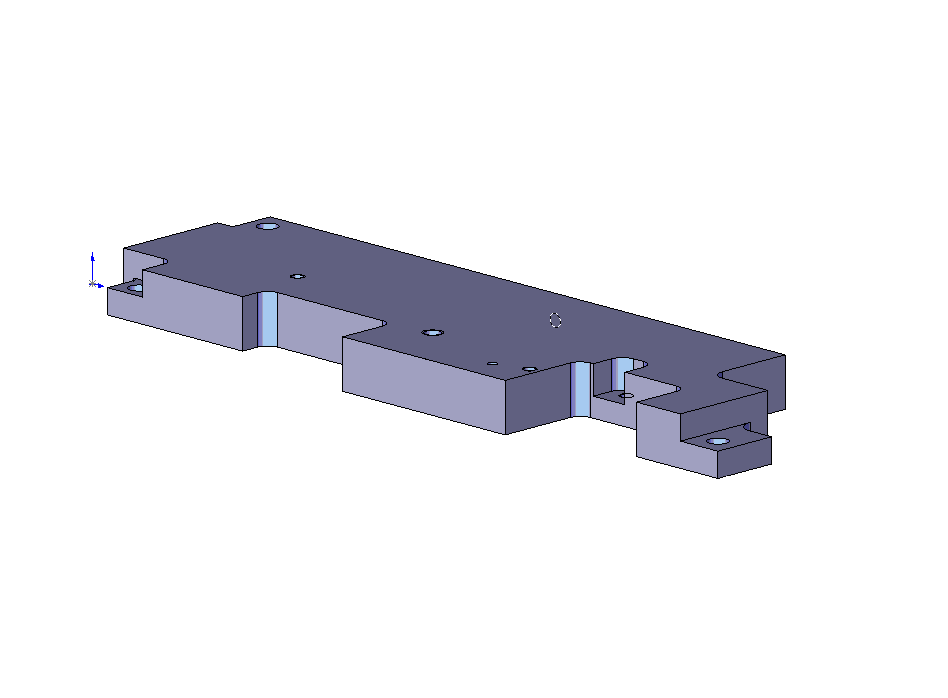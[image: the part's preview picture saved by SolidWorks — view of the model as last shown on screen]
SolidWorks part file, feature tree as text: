
SOLIDWORKS PART (.sldprt)
format: sldprt  version: not decoded by parser v0  size: 2,328,576 bytes
history: native  units: mm
features: sketch x30, cut_extrude x15, hole x6, thread x5, extrude x3, material x1, fillet x1 (+12 scaffold rows collapsed)
feature tree (73):
  scaffold x12  (default folders/planes/origin — collapsed)
  material  "Material <not specified>"
  sketch  "Sketch1"  dims[D1=16.0mm D2=500.0mm]
  extrude  "Base-Extrude"  Depth=65mm
  sketch  "Sketch3"  dims[c1.D1=10.0mm c1.D2=40.0mm c2.D1=95.0mm c2.D3=80.0mm]
  cut_extrude  "Access for Blade Clamp Bolts"  [1 undecoded]
  sketch  "Sketch2"  dims[c1.D3=20.0mm c1.D4=~11.171764mm c2.D3=4.0mm c2.D1=60.0mm c2.D2=15.0mm c3.D1=45.0mm c3.D2=30.0mm c4.D1=34.595mm c4.D2=16.0mm c4.D4=45.0mm c4.D5=60.0mm c4.D6=18.0mm c5.D5=60.0mm c5.D6=32.0mm c6.D5=60.0mm c6.D6=32.0mm c7.D5=60.0mm c7.D6=18.0mm c7.D4=45.0mm c8.D5=30.0mm c9.D5=7.0deg c9.D2=400.0mm c10.D5=400.0mm c11.D5=8.5deg c11.D4=435.0mm c11.D1=38.0mm c11.D2=40.0mm c12.D2=80.5deg c12.D4=35.0mm]
  extrude  "Boss-Extrude1"  [1 undecoded]
  sketch  "Sketch4"  dims[c1.D1=45.0mm c1.D2=35.0mm c1.D3=45.0mm c2.D1=~54.083269mm c2.D3=45.0mm c2.D4=45.0mm c3.D3=45.0mm c3.D4=45.0mm c4.D3=45.0mm c4.D4=45.0mm c5.D3=45.0mm c5.D4=45.0mm c6.D3=45.0mm c6.D4=45.0mm c7.D3=45.0mm c7.D4=45.0mm c8.D3=45.0mm c8.D4=45.0mm c9.D3=45.0mm c9.D4=45.0mm c10.D3=45.0mm c10.D4=45.0mm c11.D3=45.0mm c11.D4=45.0mm c12.D3=45.0mm c12.D4=45.0mm c13.D3=45.0mm c13.D4=45.0mm c14.D3=45.0mm c14.D4=45.0mm c15.D3=45.0mm c15.D4=45.0mm c16.D3=45.0mm c16.D4=45.0mm c17.D3=45.0mm c17.D1=45.0mm c18.D3=80.0mm]
  cut_extrude  "Cut-Extrude3"  [1 undecoded]
  sketch  "Sketch5"  dims[c1.D5=4.0mm c1.D1=100.0mm c1.D2=10.0mm c1.D3=10.0mm c2.D2=10.0mm c2.D4=40.0mm c2.D5=~38.907493mm c2.D6=~38.914066mm c3.D4=40.0mm c3.D2=40.0mm c4.D4=10.0mm]
  cut_extrude  "Cut-Extrude4"  [1 undecoded]
  sketch  "Sketch6"
  cut_extrude  "Cut-Extrude5"  [1 undecoded]
  sketch  "Sketch7"  dims[D1=10.0mm]
  extrude  "Extrude1"  [1 undecoded]
  sketch  "Sketch8"  dims[D1=4.0mm D2=65.0mm D3=42.5mm D4=30.0mm D5=10.0mm]
  cut_extrude  "Cut-Extrude6"  [1 undecoded]
  sketch  "Sketch9"
  cut_extrude  "Cut-Extrude7"  [1 undecoded]
  sketch  "Sketch10"
  cut_extrude  "Cut-Extrude8"  [1 undecoded]
  sketch  "Sketch12"  dims[c1.D1=2.8448mm c1.D3=4.1656mm c1.D2=10.0mm c2.D3=160.0mm]
  cut_extrude  "Holes for Flag"  [1 undecoded]
  sketch  "Sketch14"  dims[D1=120.0mm D2=27.5mm]
  cut_extrude  "Angled Cut"  [1 undecoded]
  hole  "1/4 Clearance Hole1"  Diameter=6.5278mm Depth=16mm
  sketch  "Sketch16"  dims[D1=12.5mm D2=7.5mm D3=6.0mm D4=12.5mm D5=20.0mm D6=7.5mm D7=7.5mm]
  sketch  "Sketch15"  dims[hole-wizard template sketch: 60 standard entries collapsed; hole parameters kept: c18.Thru Hole Depth=16.0mm]
  sketch  "Sketch17"  dims[D3=2.0mm D6=2.0mm D1=6.0mm D2=12.5mm D4=15.0mm D5=6.0mm]
  cut_extrude  "Cut-Extrude9"  [1 undecoded]
  hole  "#8-32 Tapped Hole2"  [1 undecoded]
  sketch  "3DSketch1"  dims[c1.D1=13.25mm c1.D2=~5.139942mm c1.D3=5.0mm c2.D2=78.5mm]
  thread  "Cosmetic Thread1"  Diameter=4.1656mm  [1 undecoded]
  sketch  "Sketch20"  dims[hole-wizard template sketch: 60 standard entries collapsed; hole parameters kept: c18.Thru Tap Drill Depth=16.0mm]
  sketch  "Sketch21"  dims[c1.D2=4.0mm c1.D1=20.0mm c2.D2=20.0mm]
  cut_extrude  "Cut-Extrude10"  Depth=8mm
  hole  "#8-32 Tapped Hole3"  Diameter=3.4544mm Depth=16mm
  sketch  "Sketch23"  dims[D1=194.0mm D2=39.0mm]
  sketch  "Sketch22"  dims[hole-wizard template sketch: 60 standard entries collapsed; hole parameters kept: c18.Thru Tap Drill Depth=16.0mm]
  thread  "Cosmetic Thread2"  Diameter=8.3312mm  [1 undecoded]
  hole  "1/4-20 Tapped Hole1"  Diameter=5.1054mm Depth=16mm
  sketch  "3DSketch2"  dims[D1=54.0mm D2=125.0mm]
  sketch  "Sketch25"  dims[hole-wizard template sketch: 60 standard entries collapsed; hole parameters kept: c18.Thru Tap Drill Depth=16.0mm]
  thread  "Cosmetic Thread3"  Diameter=6.35mm  [1 undecoded]
  hole  "#8-32 Tapped Hole4"  Diameter=3.4544mm Depth=12.2936mm
  sketch  "Sketch27"  dims[D1=130.0mm D2=8.0mm]
  sketch  "Sketch26"  dims[hole-wizard template sketch: 47 standard entries collapsed; hole parameters kept: c15.Tap Drill Depth=12.2936mm c15.D3=~14.816244mm c15.Drill Angle=118.0deg]
  thread  "Cosmetic Thread4"  Diameter=8.3312mm  [1 undecoded]
  hole  "#8-32 Tapped Hole5"  Diameter=3.4544mm Depth=16mm
  sketch  "Sketch29"  dims[D1=38.1mm D2=63.5mm]
  sketch  "Sketch28"  dims[hole-wizard template sketch: 60 standard entries collapsed; hole parameters kept: c18.Thru Tap Drill Depth=16.0mm]
  thread  "Cosmetic Thread5"  Diameter=8.3312mm ID=-1  [1 undecoded]
  sketch  "Sketch30"  dims[D1=5.08mm D2=38.1mm D3=30.0mm]
  cut_extrude  "Cut-Extrude11"  [1 undecoded]
  sketch  "Sketch31"  dims[D1=15.0mm]
  cut_extrude  "Cut-Extrude12"  [1 undecoded]
  sketch  "Sketch32"  dims[c1.D2=3.4544mm c1.D3=3.4544mm c1.D1=6.35mm c2.D2=6.35mm c2.D3=4.85mm]
  cut_extrude  "Cut-Extrude13"  Depth=9.525mm
  sketch  "Sketch33"  dims[D1=12.0mm D2=6.35mm]
  cut_extrude  "Cut-Extrude14"  [1 undecoded]
  fillet  "Fillet1"  Radius=4.5mm
decode coverage: 41 of 60 modeling features carry decoded parameters
note: ~ marks probable driven/reference dimensions
note: 21 parameter values undecoded
summary: no parameter record found for 16 features; Diameter pulled from absorbed wizard sketch
note: suppression state not decoded; provenance and decode notes live in map.json
